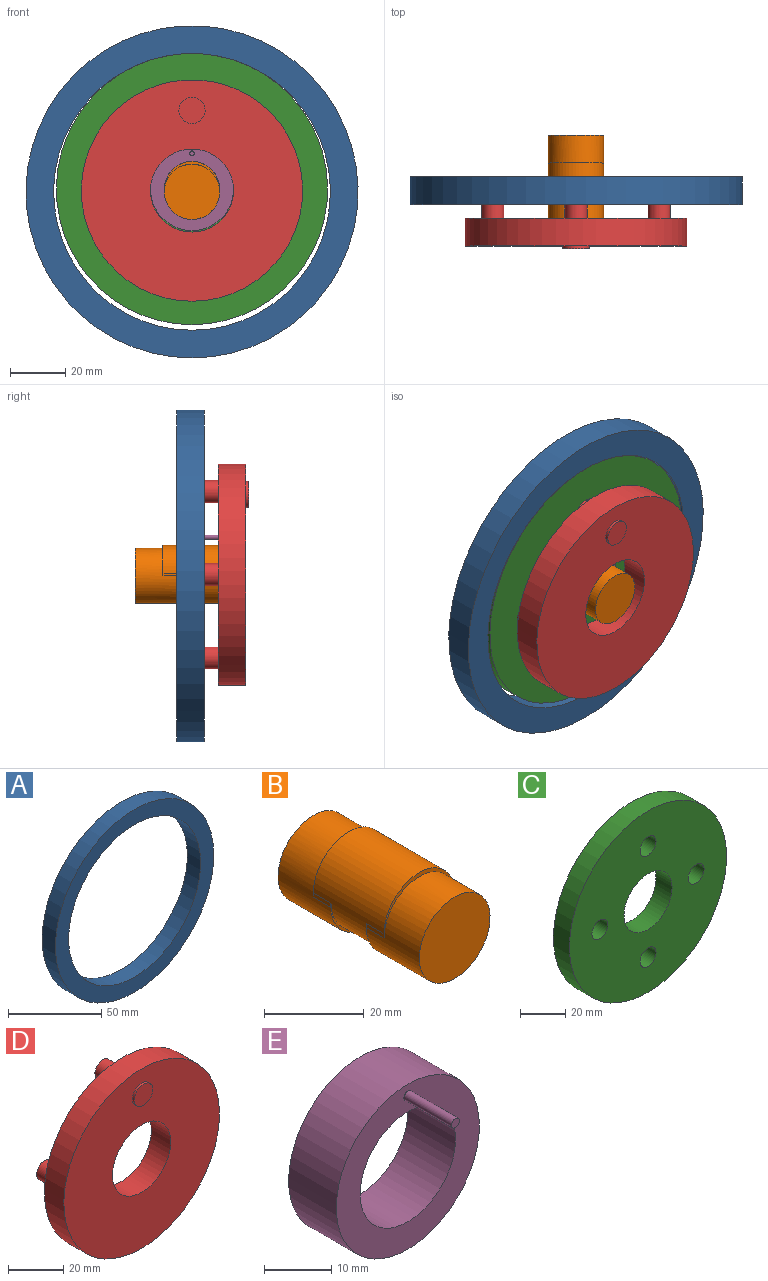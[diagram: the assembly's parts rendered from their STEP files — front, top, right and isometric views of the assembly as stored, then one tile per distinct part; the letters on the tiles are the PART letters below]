
ASSEMBLY  parts=5 mates=5
PART A: 4 faces, bbox 120x10x120 mm
  f0: cylinder r=50mm len=100mm, axis (0,1,0), area 3141.6mm2, adj f2,f3
  f1: cylinder r=60mm len=120mm, axis (0,1,0), area 3769.9mm2, adj f2,f3
  f2: plane 120x120mm, normal (0,-1,0), area 3455.8mm2, adj f0,f1
  f3: plane 120x120mm, normal (0,1,0), area 3455.8mm2, adj f0,f1
PART B: 13 faces, bbox 20x40x21 mm
  f0: cylinder r=10mm len=20mm, axis (0,1,0), area 785.4mm2, adj f1,f2,f3,f5,f6
  f1: plane 20x20mm, normal (0,1,0), area 314.2mm2, adj f0
  f2: plane 20x11mm, normal (0,1,0), area 20mm2, adj f0,f3,f4,f5
  f3: plane 5x1mm, normal (1,0,0), area 5mm2, adj f0,f2,f4,f6
  f4: cylinder r=10mm len=20mm, axis (0,1,0), area 942.5mm2, adj f2,f3,f5,f6,f9,f10,f11,f12
  f5: plane 5x1mm, normal (-1,0,0), area 5mm2, adj f0,f2,f4,f6
  f6: plane 20x11mm, normal (0,-1,0), area 20mm2, adj f0,f3,f4,f5
  f7: cylinder r=10mm len=20mm, axis (0,-1,0), area 785.4mm2, adj f8,f9,f10,f11,f12
  f8: plane 20x20mm, normal (0,-1,0), area 314.2mm2, adj f7
  f9: plane 20x11mm, normal (0,-1,0), area 20mm2, adj f4,f7,f10,f11
  f10: plane 5x1mm, normal (1,0,0), area 5mm2, adj f4,f7,f9,f12
  f11: plane 5x1mm, normal (-1,0,0), area 5mm2, adj f4,f7,f9,f12
  f12: plane 20x11mm, normal (0,1,0), area 20mm2, adj f4,f7,f10,f11
PART C: 8 faces, bbox 98x10x98 mm
  f0: cylinder r=5mm len=10mm, axis (0,-1,0), area 314.2mm2, adj f5,f6
  f1: cylinder r=5mm len=10mm, axis (0,-1,0), area 314.2mm2, adj f5,f6
  f2: cylinder r=5mm len=10mm, axis (0,-1,0), area 314.2mm2, adj f5,f6
  f3: cylinder r=15mm len=30mm, axis (0,1,0), area 942.5mm2, adj f5,f6
  f4: cylinder r=49mm len=98mm, axis (0,1,0), area 3078.8mm2, adj f5,f6
  f5: plane 98x98mm, normal (0,-1,0), area 6521.9mm2, adj f0,f1,f2,f3,f4,f7
  f6: plane 98x98mm, normal (0,1,0), area 6521.9mm2, adj f0,f1,f2,f3,f4,f7
  f7: cylinder r=5mm len=10mm, axis (0,-1,0), area 314.2mm2, adj f5,f6
PART D: 14 faces, bbox 80x21x80 mm
  f0: cylinder r=4mm len=10mm, axis (0,-1,0), area 251.3mm2, adj f1,f8
  f1: plane 8x8mm, normal (0,1,0), area 50.3mm2, adj f0
  f2: cylinder r=4mm len=10mm, axis (0,-1,0), area 251.3mm2, adj f3,f8
  f3: plane 8x8mm, normal (0,1,0), area 50.3mm2, adj f2
  f4: cylinder r=4mm len=10mm, axis (0,-1,0), area 251.3mm2, adj f5,f8
  f5: plane 8x8mm, normal (0,1,0), area 50.3mm2, adj f4
  f6: cylinder r=15mm len=30mm, axis (0,-1,0), area 942.5mm2, adj f8,f9
  f7: cylinder r=40mm len=80mm, axis (0,-1,0), area 2513.3mm2, adj f8,f9
  f8: plane 80x80mm, normal (0,1,0), area 4118.6mm2, adj f0,f2,f4,f6,f7,f10
  f9: plane 80x80mm, normal (0,-1,0), area 4249.3mm2, adj f6,f7,f12
  f10: cylinder r=4mm len=10mm, axis (0,-1,0), area 251.3mm2, adj f8,f11
  f11: plane 8x8mm, normal (0,1,0), area 50.3mm2, adj f10
  f12: cylinder r=4.73mm len=9.46mm, axis (0,1,0), area 29.7mm2, adj f9,f13
  f13: plane 9.46x9.46mm, normal (0,-1,0), area 70.3mm2, adj f12
PART E: 6 faces, bbox 30x20x30 mm
  f0: plane 30x30mm, normal (0,-1,0), area 390.6mm2, adj f1,f2,f4
  f1: cylinder r=10mm len=20mm, axis (0,1,0), area 628.3mm2, adj f0,f3
  f2: cylinder r=15mm len=30mm, axis (0,1,0), area 942.5mm2, adj f0,f3
  f3: plane 30x30mm, normal (0,1,0), area 392.7mm2, adj f1,f2
  f4: cylinder r=0.82mm len=10mm, axis (0,1,0), area 51.5mm2, adj f0,f5
  f5: plane 1.64x1.64mm, normal (0,-1,0), area 2.1mm2, adj f4
PLACE A t=(0,-15,0)mm
PLACE B at identity
PLACE C t=(0,-15,1)mm
PLACE D t=(0,0,0.48)mm
PLACE E t=(0,-15,1)mm
MATE parallel E.f4 <-> A.f1  axis (0,-1,0) through (0,-25,13.94)mm
MATE parallel D.f9 <-> C.f4  axis (0,-1,0) through (0,-40,0)mm
MATE revolute B.f4 <-> E.f1  axis (0,1,0) through (0,-20,1)mm
MATE revolute C.f3 <-> E.f2  axis (0,1,0) through (0,-20,1)mm
MATE revolute D.f9 <-> B.f0  axis (0,-1,0) through (0,-40,0)mm
